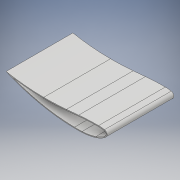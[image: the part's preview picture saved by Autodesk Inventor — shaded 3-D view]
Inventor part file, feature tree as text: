
AUTODESK INVENTOR PART (.ipt)
format: ipt  version: 2018.2 (Build 222227000, 227)  size: 139,776 bytes
history: native  units: mm
features: extrude x1, shell x1, sketch x1, projected_geometry x1
ambient origin geometry x8: Origin, YZ Plane, XZ Plane, XY Plane, X Axis, Y Axis, Z Axis, Center Point
bodies: Body1 (feature_tree)
feature tree (4):
  extrude  "押し出し1"  Depth=225.0mm TaperAngle=0.0deg
  shell  "シェル1"  Thickness=3.0mm
  sketch  "スケッチ1"
  projected_geometry  "投影ループ1"
